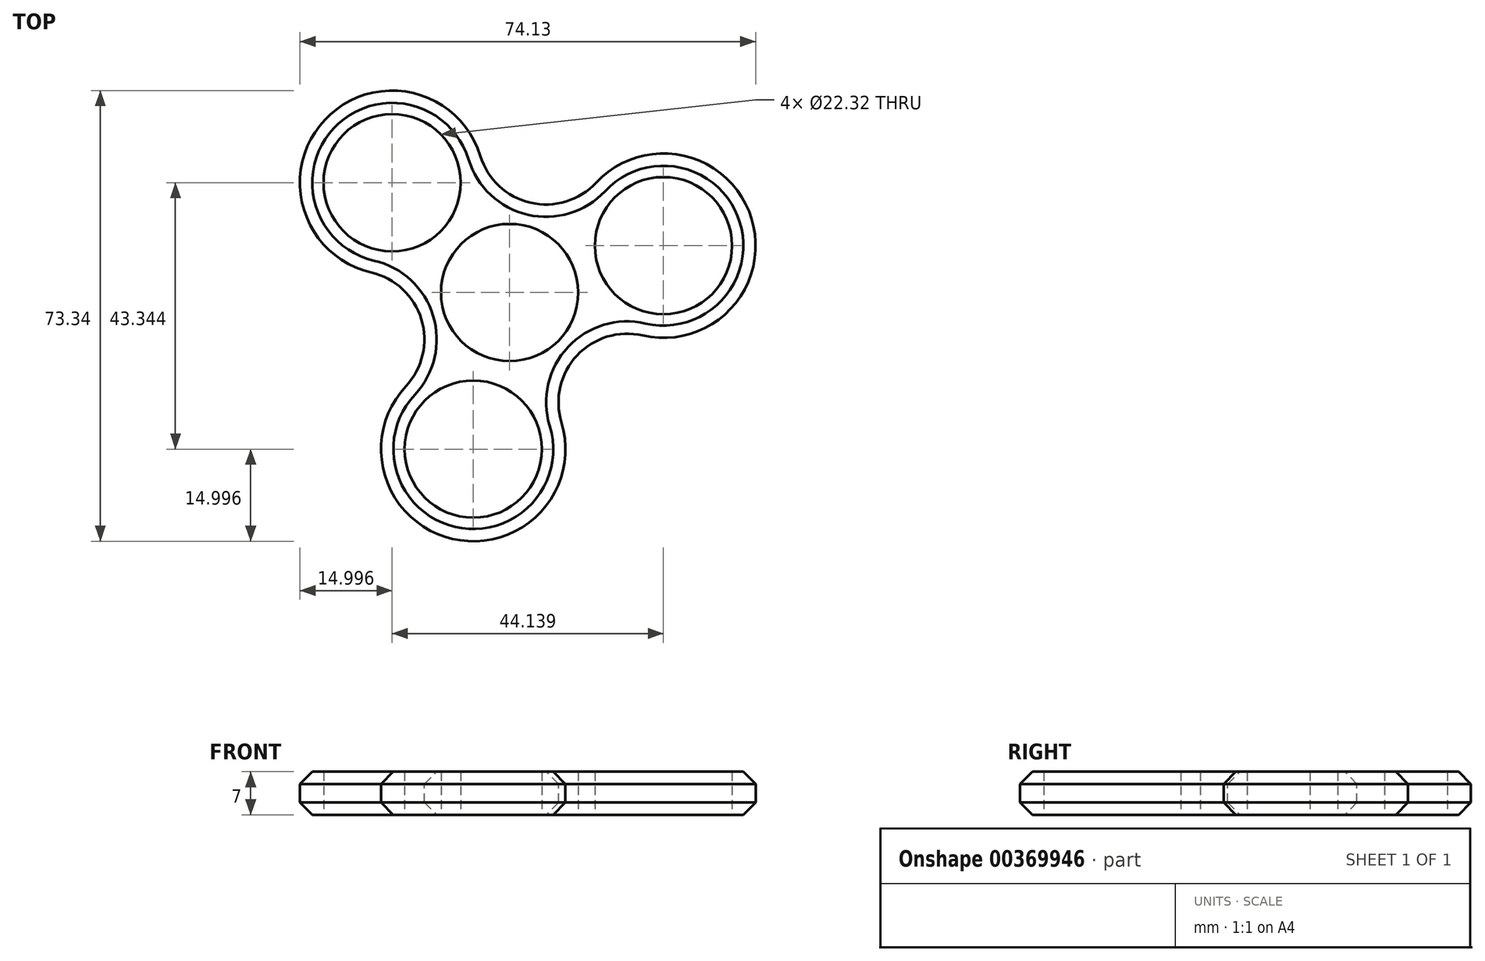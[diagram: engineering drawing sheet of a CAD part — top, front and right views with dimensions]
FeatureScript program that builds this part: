
annotation { "Feature Type Name" : "Feature", "Feature Type Description" : "" }
export const myFeature = defineFeature(function(context is Context, id is Id, definition is map)
    precondition{}
    {
        {
            var Q0;
            Q0=qCreatedBy(makeId("Top.planeOp"),FACE);
            var sketch = newSketch(context, id + "F0", { "sketchPlane" : qUnion([Q0])});
            skCircle(sketch, "E0", {"center": v(0, 0) * mm, "radius": 11.16 * mm});
            skLineSegment(sketch, "E1", {"start": v(0, 0) * mm, "end": v(-19.11, 17.86) * mm});
            skLineSegment(sketch, "E2", {"start": v(0, 0) * mm, "end": v(25.02, 7.62) * mm});
            skLineSegment(sketch, "E3", {"start": v(0, 0) * mm, "end": v(-5.91, -25.48) * mm});
            skCircle(sketch, "E4", {"center": v(-19.11, 17.86) * mm, "radius": 11.16 * mm});
            skCircle(sketch, "E5", {"center": v(25.02, 7.62) * mm, "radius": 11.16 * mm});
            skCircle(sketch, "E6", {"center": v(-5.91, -25.48) * mm, "radius": 11.16 * mm});
            skCircle(sketch, "E7", {"center": v(0, 0) * mm, "radius": 15 * mm});
            skCircle(sketch, "E8", {"center": v(-19.11, 17.86) * mm, "radius": 15 * mm});
            skCircle(sketch, "E9", {"center": v(25.02, 7.62) * mm, "radius": 15 * mm});
            skCircle(sketch, "E10", {"center": v(-5.91, -25.48) * mm, "radius": 15 * mm});
            skLineSegment(sketch, "E11", {"start": v(-19.11, 17.86) * mm, "end": v(-8.87, 28.82) * mm});
            skLineSegment(sketch, "E12", {"start": v(25.02, 7.62) * mm, "end": v(20.65, 21.97) * mm});
            skLineSegment(sketch, "E13", {"start": v(-5.91, -25.48) * mm, "end": v(8.7, -28.87) * mm});
            skLineSegment(sketch, "E14", {"start": v(-5.91, -25.48) * mm, "end": v(-20.52, -22.1) * mm});
            skLineSegment(sketch, "E15", {"start": v(-19.11, 17.86) * mm, "end": v(-29.36, 6.9) * mm});
            skLineSegment(sketch, "E16", {"start": v(25.02, 7.62) * mm, "end": v(29.4, -6.73) * mm});
            skArc(sketch, "E17", {"start": v(-8.87, 28.82) * mm, "mid": v(3.39, 14.61) * mm, "end": v(20.65, 21.97) * mm});
            skArc(sketch, "E18", {"start": v(-20.52, -22.1) * mm, "mid": v(-14.35, -4.37) * mm, "end": v(-29.36, 6.9) * mm});
            skArc(sketch, "E19", {"start": v(29.4, -6.73) * mm, "mid": v(10.96, -10.24) * mm, "end": v(8.7, -28.87) * mm});
            skSolve(sketch);
        }
        {
            var Q0;
            {var subQ0=sQuery(id+"F0.wireOp",EDGE,"E15");var subQ1=sQuery(id+"F0.wireOp",EDGE,"E4");var subQ2=makeQuery(id+"F0.imprint","INTERSECT",VERTEX,{"derivedFrom":[subQ1,subQ0]});Q0=makeQuery(id+"F0.imprint","IMPRINT",FACE,{"disambiguationData":[TD([[makeQuery(id+"F0.imprint","IMPRINT",EDGE,{"disambiguationData":[TD([[subQ2,1.0]])],"derivedFrom":subQ1}),-1.0]])]});}
            var Q1;
            {var subQ0=sQuery(id+"F0.wireOp",EDGE,"E17");var subQ1=sQuery(id+"F0.wireOp",EDGE,"E8");var subQ3=makeQuery(id+"F0.imprint","INTERSECT",VERTEX,{"derivedFrom":[subQ1,subQ0]});Q1=makeQuery(id+"F0.imprint","IMPRINT",FACE,{"disambiguationData":[TD([[makeQuery(id+"F0.imprint","IMPRINT",EDGE,{"disambiguationData":[TD([[subQ3,-1.0]])],"derivedFrom":subQ1}),1.0]])]});}
            var Q2;
            {var subQ0=sQuery(id+"F0.wireOp",EDGE,"E17");var subQ2=sQuery(id+"F0.wireOp",EDGE,"E8");var subQ6=makeQuery(id+"F0.imprint","INTERSECT",VERTEX,{"derivedFrom":[subQ2,subQ0]});Q2=makeQuery(id+"F0.imprint","IMPRINT",FACE,{"disambiguationData":[TD([[makeQuery(id+"F0.imprint","IMPRINT",EDGE,{"disambiguationData":[TD([[subQ6,1.0]])],"derivedFrom":subQ2}),1.0]])]});}
            var Q3;
            {var subQ0=sQuery(id+"F0.wireOp",EDGE,"E8");var subQ3=sQuery(id+"F0.wireOp",EDGE,"E7");var subQ5=makeQuery(id+"F0.imprint","INTERSECT",VERTEX,{"disambiguationData":[OD(0.0)],"derivedFrom":[subQ3,subQ0]});Q3=makeQuery(id+"F0.imprint","IMPRINT",FACE,{"disambiguationData":[TD([[makeQuery(id+"F0.imprint","IMPRINT",EDGE,{"disambiguationData":[TD([[subQ5,-1.0]])],"derivedFrom":subQ3}),1.0]])]});}
            var Q4;
            {var subQ0=sQuery(id+"F0.wireOp",EDGE,"E8");var subQ3=sQuery(id+"F0.wireOp",EDGE,"E7");var subQ5=makeQuery(id+"F0.imprint","INTERSECT",VERTEX,{"disambiguationData":[OD(1.0)],"derivedFrom":[subQ3,subQ0]});Q4=makeQuery(id+"F0.imprint","IMPRINT",FACE,{"disambiguationData":[TD([[makeQuery(id+"F0.imprint","IMPRINT",EDGE,{"disambiguationData":[TD([[subQ5,1.0]])],"derivedFrom":subQ3}),1.0]])]});}
            var Q5;
            {var subQ0=sQuery(id+"F0.wireOp",EDGE,"E18");var subQ1=sQuery(id+"F0.wireOp",EDGE,"E8");var subQ2=makeQuery(id+"F0.imprint","INTERSECT",VERTEX,{"derivedFrom":[subQ1,subQ0]});Q5=makeQuery(id+"F0.imprint","IMPRINT",FACE,{"disambiguationData":[TD([[makeQuery(id+"F0.imprint","IMPRINT",EDGE,{"disambiguationData":[TD([[subQ2,-1.0]])],"derivedFrom":subQ1}),1.0]])]});}
            var Q6;
            {var subQ0=sQuery(id+"F0.wireOp",EDGE,"E18");var subQ1=sQuery(id+"F0.wireOp",EDGE,"E8");var subQ3=makeQuery(id+"F0.imprint","INTERSECT",VERTEX,{"derivedFrom":[subQ1,subQ0]});Q6=makeQuery(id+"F0.imprint","IMPRINT",FACE,{"disambiguationData":[TD([[makeQuery(id+"F0.imprint","IMPRINT",EDGE,{"disambiguationData":[TD([[subQ3,1.0]])],"derivedFrom":subQ1}),1.0]])]});}
            var Q7;
            {var subQ0=sQuery(id+"F0.wireOp",EDGE,"E18");var subQ1=sQuery(id+"F0.wireOp",EDGE,"E10");var subQ3=makeQuery(id+"F0.imprint","INTERSECT",VERTEX,{"derivedFrom":[subQ1,subQ0]});Q7=makeQuery(id+"F0.imprint","IMPRINT",FACE,{"disambiguationData":[TD([[makeQuery(id+"F0.imprint","IMPRINT",EDGE,{"disambiguationData":[TD([[subQ3,-1.0]])],"derivedFrom":subQ1}),1.0]])]});}
            var Q8;
            {var subQ0=sQuery(id+"F0.wireOp",EDGE,"E18");var subQ2=sQuery(id+"F0.wireOp",EDGE,"E10");var subQ6=makeQuery(id+"F0.imprint","INTERSECT",VERTEX,{"derivedFrom":[subQ2,subQ0]});Q8=makeQuery(id+"F0.imprint","IMPRINT",FACE,{"disambiguationData":[TD([[makeQuery(id+"F0.imprint","IMPRINT",EDGE,{"disambiguationData":[TD([[subQ6,1.0]])],"derivedFrom":subQ2}),1.0]])]});}
            var Q9;
            {var subQ0=sQuery(id+"F0.wireOp",EDGE,"E10");var subQ3=sQuery(id+"F0.wireOp",EDGE,"E7");var subQ5=makeQuery(id+"F0.imprint","INTERSECT",VERTEX,{"disambiguationData":[OD(0.0)],"derivedFrom":[subQ3,subQ0]});Q9=makeQuery(id+"F0.imprint","IMPRINT",FACE,{"disambiguationData":[TD([[makeQuery(id+"F0.imprint","IMPRINT",EDGE,{"disambiguationData":[TD([[subQ5,-1.0]])],"derivedFrom":subQ3}),1.0]])]});}
            var Q10;
            {var subQ0=sQuery(id+"F0.wireOp",EDGE,"E10");var subQ3=sQuery(id+"F0.wireOp",EDGE,"E7");var subQ5=makeQuery(id+"F0.imprint","INTERSECT",VERTEX,{"disambiguationData":[OD(1.0)],"derivedFrom":[subQ3,subQ0]});Q10=makeQuery(id+"F0.imprint","IMPRINT",FACE,{"disambiguationData":[TD([[makeQuery(id+"F0.imprint","IMPRINT",EDGE,{"disambiguationData":[TD([[subQ5,1.0]])],"derivedFrom":subQ3}),1.0]])]});}
            var Q11;
            {var subQ0=sQuery(id+"F0.wireOp",EDGE,"E19");var subQ1=sQuery(id+"F0.wireOp",EDGE,"E10");var subQ3=makeQuery(id+"F0.imprint","INTERSECT",VERTEX,{"derivedFrom":[subQ1,subQ0]});Q11=makeQuery(id+"F0.imprint","IMPRINT",FACE,{"disambiguationData":[TD([[makeQuery(id+"F0.imprint","IMPRINT",EDGE,{"disambiguationData":[TD([[subQ3,1.0]])],"derivedFrom":subQ1}),1.0]])]});}
            var Q12;
            {var subQ0=sQuery(id+"F0.wireOp",EDGE,"E19");var subQ1=sQuery(id+"F0.wireOp",EDGE,"E10");var subQ2=makeQuery(id+"F0.imprint","INTERSECT",VERTEX,{"derivedFrom":[subQ1,subQ0]});Q12=makeQuery(id+"F0.imprint","IMPRINT",FACE,{"disambiguationData":[TD([[makeQuery(id+"F0.imprint","IMPRINT",EDGE,{"disambiguationData":[TD([[subQ2,-1.0]])],"derivedFrom":subQ1}),1.0]])]});}
            var Q13;
            {var subQ0=sQuery(id+"F0.wireOp",EDGE,"E14");var subQ1=sQuery(id+"F0.wireOp",EDGE,"E6");var subQ2=makeQuery(id+"F0.imprint","INTERSECT",VERTEX,{"derivedFrom":[subQ1,subQ0]});Q13=makeQuery(id+"F0.imprint","IMPRINT",FACE,{"disambiguationData":[TD([[makeQuery(id+"F0.imprint","IMPRINT",EDGE,{"disambiguationData":[TD([[subQ2,-1.0]])],"derivedFrom":subQ1}),-1.0]])]});}
            var Q14;
            {var subQ1=sQuery(id+"F0.wireOp",EDGE,"E7");var subQ5=makeQuery(id+"F0.imprint","INTERSECT",VERTEX,{"derivedFrom":[subQ1,sQuery(id+"F0.wireOp",EDGE,"E18")]});Q14=makeQuery(id+"F0.imprint","IMPRINT",FACE,{"disambiguationData":[TD([[makeQuery(id+"F0.imprint","IMPRINT",EDGE,{"disambiguationData":[TD([[subQ5,1.0]])],"derivedFrom":subQ1}),1.0]])]});}
            var Q15;
            {var subQ1=sQuery(id+"F0.wireOp",EDGE,"E7");var subQ5=makeQuery(id+"F0.imprint","INTERSECT",VERTEX,{"derivedFrom":[subQ1,sQuery(id+"F0.wireOp",EDGE,"E19")]});Q15=makeQuery(id+"F0.imprint","IMPRINT",FACE,{"disambiguationData":[TD([[makeQuery(id+"F0.imprint","IMPRINT",EDGE,{"disambiguationData":[TD([[subQ5,1.0]])],"derivedFrom":subQ1}),1.0]])]});}
            var Q16;
            {var subQ0=sQuery(id+"F0.wireOp",EDGE,"E9");var subQ3=sQuery(id+"F0.wireOp",EDGE,"E7");var subQ5=makeQuery(id+"F0.imprint","INTERSECT",VERTEX,{"disambiguationData":[OD(1.0)],"derivedFrom":[subQ3,subQ0]});Q16=makeQuery(id+"F0.imprint","IMPRINT",FACE,{"disambiguationData":[TD([[makeQuery(id+"F0.imprint","IMPRINT",EDGE,{"disambiguationData":[TD([[subQ5,-1.0]])],"derivedFrom":subQ3}),1.0]])]});}
            var Q17;
            {var subQ0=sQuery(id+"F0.wireOp",EDGE,"E9");var subQ3=sQuery(id+"F0.wireOp",EDGE,"E7");var subQ5=makeQuery(id+"F0.imprint","INTERSECT",VERTEX,{"disambiguationData":[OD(0.0)],"derivedFrom":[subQ3,subQ0]});Q17=makeQuery(id+"F0.imprint","IMPRINT",FACE,{"disambiguationData":[TD([[makeQuery(id+"F0.imprint","IMPRINT",EDGE,{"disambiguationData":[TD([[subQ5,1.0]])],"derivedFrom":subQ3}),1.0]])]});}
            var Q18;
            {var subQ1=sQuery(id+"F0.wireOp",EDGE,"E7");var subQ5=makeQuery(id+"F0.imprint","INTERSECT",VERTEX,{"derivedFrom":[subQ1,sQuery(id+"F0.wireOp",EDGE,"E17")]});Q18=makeQuery(id+"F0.imprint","IMPRINT",FACE,{"disambiguationData":[TD([[makeQuery(id+"F0.imprint","IMPRINT",EDGE,{"disambiguationData":[TD([[subQ5,1.0]])],"derivedFrom":subQ1}),1.0]])]});}
            var Q19;
            {var subQ0=sQuery(id+"F0.wireOp",EDGE,"E17");var subQ2=sQuery(id+"F0.wireOp",EDGE,"E9");var subQ6=makeQuery(id+"F0.imprint","INTERSECT",VERTEX,{"derivedFrom":[subQ2,subQ0]});Q19=makeQuery(id+"F0.imprint","IMPRINT",FACE,{"disambiguationData":[TD([[makeQuery(id+"F0.imprint","IMPRINT",EDGE,{"disambiguationData":[TD([[subQ6,-1.0]])],"derivedFrom":subQ2}),1.0]])]});}
            var Q20;
            {var subQ0=sQuery(id+"F0.wireOp",EDGE,"E17");var subQ1=sQuery(id+"F0.wireOp",EDGE,"E9");var subQ3=makeQuery(id+"F0.imprint","INTERSECT",VERTEX,{"derivedFrom":[subQ1,subQ0]});Q20=makeQuery(id+"F0.imprint","IMPRINT",FACE,{"disambiguationData":[TD([[makeQuery(id+"F0.imprint","IMPRINT",EDGE,{"disambiguationData":[TD([[subQ3,1.0]])],"derivedFrom":subQ1}),1.0]])]});}
            var Q21;
            {var subQ0=sQuery(id+"F0.wireOp",EDGE,"E12");var subQ1=sQuery(id+"F0.wireOp",EDGE,"E5");var subQ2=makeQuery(id+"F0.imprint","INTERSECT",VERTEX,{"derivedFrom":[subQ1,subQ0]});Q21=makeQuery(id+"F0.imprint","IMPRINT",FACE,{"disambiguationData":[TD([[makeQuery(id+"F0.imprint","IMPRINT",EDGE,{"disambiguationData":[TD([[subQ2,1.0]])],"derivedFrom":subQ1}),-1.0]])]});}
            var Q22;
            {var subQ0=sQuery(id+"F0.wireOp",EDGE,"E19");var subQ2=sQuery(id+"F0.wireOp",EDGE,"E9");var subQ9=makeQuery(id+"F0.imprint","INTERSECT",VERTEX,{"derivedFrom":[subQ2,subQ0]});Q22=makeQuery(id+"F0.imprint","IMPRINT",FACE,{"disambiguationData":[TD([[makeQuery(id+"F0.imprint","IMPRINT",EDGE,{"disambiguationData":[TD([[subQ9,1.0]])],"derivedFrom":subQ2}),1.0]])]});}
            var Q23;
            {var subQ0=sQuery(id+"F0.wireOp",EDGE,"E19");var subQ1=sQuery(id+"F0.wireOp",EDGE,"E9");var subQ3=makeQuery(id+"F0.imprint","INTERSECT",VERTEX,{"derivedFrom":[subQ1,subQ0]});Q23=makeQuery(id+"F0.imprint","IMPRINT",FACE,{"disambiguationData":[TD([[makeQuery(id+"F0.imprint","IMPRINT",EDGE,{"disambiguationData":[TD([[subQ3,-1.0]])],"derivedFrom":subQ1}),1.0]])]});}
            extrude(context, id + "F1", {"entities" : qUnion([Q0, Q1, Q2, Q3, Q4, Q5, Q6, Q7, Q8, Q9, Q10, Q11, Q12, Q13, Q14, Q15, Q16, Q17, Q18, Q19, Q20, Q21, Q22, Q23]), "depth" : 7 * mm, "offsetDistance" : 25 * mm});
        }
        {
            var Q0;
            {var subQ0=sQuery(id+"F0.wireOp",EDGE,"E8");var subQ1=sQuery(id+"F0.wireOp",EDGE,"E7");Q0=makeQuery(id+"F1.opExtrude","SWEPT_EDGE",EDGE,{"disambiguationData":[OSD([subQ1,subQ0]),TDD([makeQuery(id+"F0.imprint","INTERSECT",VERTEX,{"disambiguationData":[OD(1.0)],"derivedFrom":[subQ1,subQ0]})])]});}
            var Q1;
            {var subQ0=sQuery(id+"F0.wireOp",EDGE,"E10");var subQ1=sQuery(id+"F0.wireOp",EDGE,"E7");Q1=makeQuery(id+"F1.opExtrude","SWEPT_EDGE",EDGE,{"disambiguationData":[OSD([subQ1,subQ0]),TDD([makeQuery(id+"F0.imprint","INTERSECT",VERTEX,{"disambiguationData":[OD(0.0)],"derivedFrom":[subQ1,subQ0]})])]});}
            var Q2;
            {var subQ0=sQuery(id+"F0.wireOp",EDGE,"E9");var subQ1=sQuery(id+"F0.wireOp",EDGE,"E7");Q2=makeQuery(id+"F1.opExtrude","SWEPT_EDGE",EDGE,{"disambiguationData":[OSD([subQ1,subQ0]),TDD([makeQuery(id+"F0.imprint","INTERSECT",VERTEX,{"disambiguationData":[OD(0.0)],"derivedFrom":[subQ1,subQ0]})])]});}
            var Q3;
            {var subQ0=sQuery(id+"F0.wireOp",EDGE,"E8");var subQ1=sQuery(id+"F0.wireOp",EDGE,"E7");Q3=makeQuery(id+"F1.opExtrude","SWEPT_EDGE",EDGE,{"disambiguationData":[OSD([subQ1,subQ0]),TDD([makeQuery(id+"F0.imprint","INTERSECT",VERTEX,{"disambiguationData":[OD(0.0)],"derivedFrom":[subQ1,subQ0]})])]});}
            var Q4;
            {var subQ0=sQuery(id+"F0.wireOp",EDGE,"E9");var subQ1=sQuery(id+"F0.wireOp",EDGE,"E7");Q4=makeQuery(id+"F1.opExtrude","SWEPT_EDGE",EDGE,{"disambiguationData":[OSD([subQ1,subQ0]),TDD([makeQuery(id+"F0.imprint","INTERSECT",VERTEX,{"disambiguationData":[OD(1.0)],"derivedFrom":[subQ1,subQ0]})])]});}
            var Q5;
            {var subQ0=sQuery(id+"F0.wireOp",EDGE,"E10");var subQ1=sQuery(id+"F0.wireOp",EDGE,"E7");Q5=makeQuery(id+"F1.opExtrude","SWEPT_EDGE",EDGE,{"disambiguationData":[OSD([subQ1,subQ0]),TDD([makeQuery(id+"F0.imprint","INTERSECT",VERTEX,{"disambiguationData":[OD(1.0)],"derivedFrom":[subQ1,subQ0]})])]});}
            fillet(context, id + "F2", {"entities" : qUnion([Q0, Q1, Q2, Q3, Q4, Q5]), "radius" : 11.16 * mm, "tangentPropagation" : true, "allowEdgeOverflow" : false});
        }
        {
            var Q0;
            Q0=makeQuery(id+"F1.opExtrude","CAP_EDGE",EDGE,{"disambiguationData":[OSD([sQuery(id+"F0.wireOp",EDGE,"E9")])],"isStart":false});
            var Q1;
            Q1=makeQuery(id+"F1.opExtrude","CAP_EDGE",EDGE,{"disambiguationData":[OSD([sQuery(id+"F0.wireOp",EDGE,"E9")])],"isStart":true});
            chamfer(context, id + "F3", {"entities" : qUnion([Q0, Q1]), "width" : 2 * mm, "tangentPropagation" : true});
        }
    });
